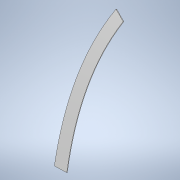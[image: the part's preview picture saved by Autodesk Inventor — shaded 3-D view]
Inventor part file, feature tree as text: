
AUTODESK INVENTOR PART (.ipt)
format: ipt  version: 2021 (Build 250183000, 183)  size: 116,224 bytes
history: native  units: in
note: dims shown in document units (in); Inventor stores cm internally (conversion verified against a paired STEP export)
features: sketch x2, sweep x1
ambient origin geometry x8: Origin, YZ Plane, XZ Plane, XY Plane, X Axis, Y Axis, Z Axis, Center Point
bodies: Solid1 (feature_tree)
feature tree (3):
  sweep  "Sweep1"
  sketch  "Sketch1"  dims[d0=2.0in d1=0.1in d4=0.0in d5=0.0in]
  sketch  "3D Sketch1"
